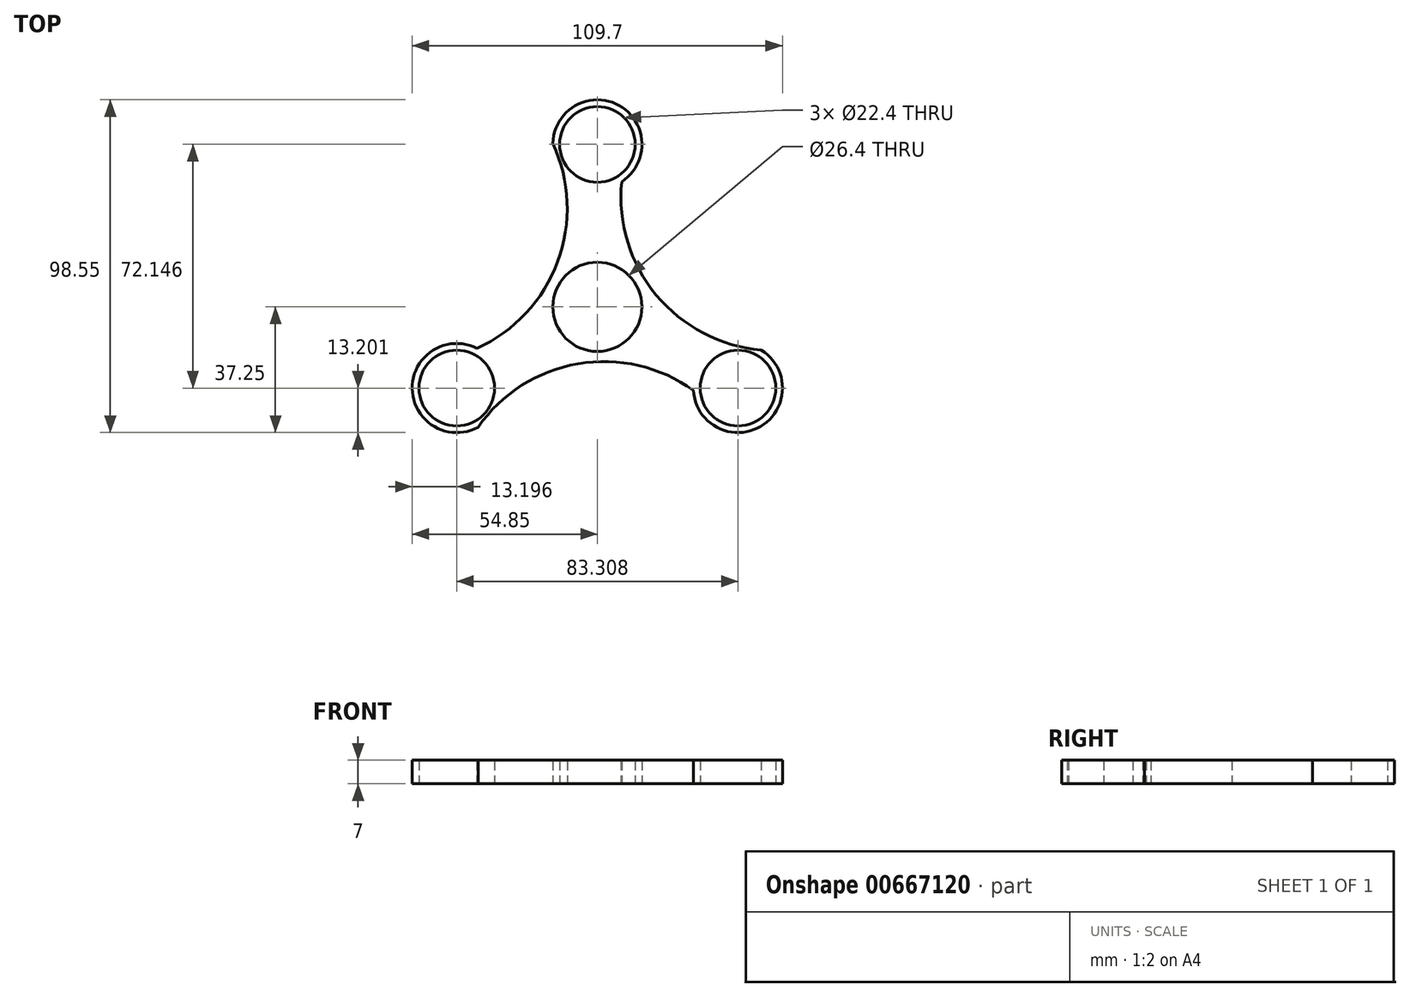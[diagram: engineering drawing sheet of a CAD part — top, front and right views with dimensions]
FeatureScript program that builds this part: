
annotation { "Feature Type Name" : "Feature", "Feature Type Description" : "" }
export const myFeature = defineFeature(function(context is Context, id is Id, definition is map)
    precondition{}
    {
        {
            var Q0;
            Q0=qCreatedBy(makeId("Top.planeOp"),FACE);
            var sketch = newSketch(context, id + "F0", { "sketchPlane" : qUnion([Q0])});
            skCircle(sketch, "E0", {"center": v(0, 0) * mm, "radius": 11.2 * mm});
            skCircle(sketch, "E1", {"center": v(0, 0) * mm, "radius": 13.2 * mm});
            skCircle(sketch, "E2", {"center": v(0, 48.1) * mm, "radius": 11.2 * mm});
            skArc(sketch, "E3", {"start": v(7.2, 37.04) * mm, "mid": v(1.96, 61.15) * mm, "end": v(-10.14, 39.64) * mm});
            skArc(sketch, "E4.1.0", {"start": v(-35.68, -12.28) * mm, "mid": v(-53.94, -28.88) * mm, "end": v(-29.26, -28.6) * mm});
            skCircle(sketch, "E4.1.1", {"center": v(-41.65, -24.05) * mm, "radius": 11.2 * mm});
            skArc(sketch, "E4.2.0", {"start": v(28.47, -24.76) * mm, "mid": v(51.98, -32.28) * mm, "end": v(39.4, -11.04) * mm});
            skCircle(sketch, "E4.2.1", {"center": v(41.65, -24.05) * mm, "radius": 11.2 * mm});
            skArc(sketch, "E5", {"start": v(-35.68, -12.28) * mm, "mid": v(-11.75, 13.38) * mm, "end": v(-13.2, 48.43) * mm});
            skArc(sketch, "E6.1.0", {"start": v(28.47, -24.76) * mm, "mid": v(-5.71, -16.86) * mm, "end": v(-35.35, -35.64) * mm});
            skArc(sketch, "E6.2.0", {"start": v(7.2, 37.04) * mm, "mid": v(17.46, 3.48) * mm, "end": v(48.54, -12.79) * mm});
            skSolve(sketch);
        }
        {
            var Q0;
            Q0=makeQuery(id+"F0.imprint","IMPRINT",FACE,{"disambiguationData":[TD([[makeQuery(id+"F0.imprint","IMPRINT",EDGE,{"derivedFrom":sQuery(id+"F0.wireOp",EDGE,"E1")}),-1.0]])]});
            extrude(context, id + "F1", {"entities" : qUnion([Q0]), "depth" : 7 * mm, "offsetDistance" : 25 * mm});
        }
    });
